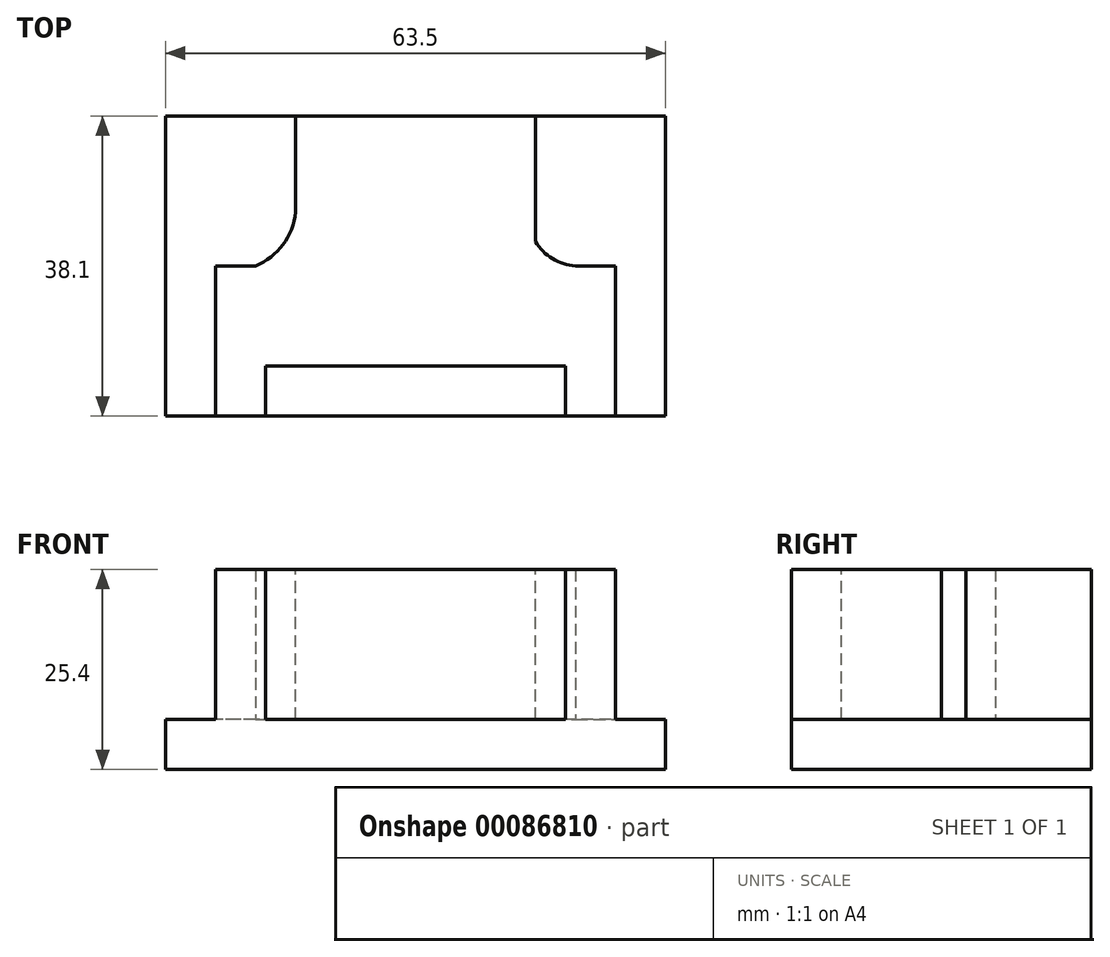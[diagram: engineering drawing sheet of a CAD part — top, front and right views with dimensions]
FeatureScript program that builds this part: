
annotation { "Feature Type Name" : "Feature", "Feature Type Description" : "" }
export const myFeature = defineFeature(function(context is Context, id is Id, definition is map)
    precondition{}
    {
        {
            var Q0;
            Q0=qCreatedBy(makeId("Top.planeOp"),FACE);
            var sketch = newSketch(context, id + "F0", { "sketchPlane" : qUnion([Q0])});
            skLineSegment(sketch, "E0", {"start": v(-31.75, 19.05) * mm, "end": v(-31.75, -19.05) * mm});
            skLineSegment(sketch, "E1", {"start": v(-31.75, -19.05) * mm, "end": v(31.75, -19.05) * mm});
            skLineSegment(sketch, "E2", {"start": v(31.75, -19.05) * mm, "end": v(31.75, 19.05) * mm});
            skLineSegment(sketch, "E3", {"start": v(31.75, 19.05) * mm, "end": v(-31.75, 19.05) * mm});
            skLineSegment(sketch, "E4", {"start": v(-31.75, 0) * mm, "end": v(31.75, 0) * mm, "construction": true});
            skLineSegment(sketch, "E5", {"start": v(0, 19.05) * mm, "end": v(0, 0) * mm, "construction": true});
            skPoint(sketch, "E6", {"position": v(0, 0) * mm});
            skSolve(sketch);
        }
        {
            var Q0;
            Q0=makeQuery(id+"F0.imprint","IMPRINT",FACE,{"disambiguationData":[TD([[makeQuery(id+"F0.imprint","IMPRINT",EDGE,{"derivedFrom":sQuery(id+"F0.wireOp",EDGE,"E0")}),1.0]])]});
            extrude(context, id + "F1", {"entities" : qUnion([Q0]), "depth" : 6.35 * mm});
        }
        {
            var Q0;
            Q0=makeQuery(id+"F1.opExtrude","CAP_FACE",FACE,{"disambiguationData":[OSD([sQuery(id+"F0.wireOp",EDGE,"E0"),sQuery(id+"F0.wireOp",EDGE,"E1"),sQuery(id+"F0.wireOp",EDGE,"E2"),sQuery(id+"F0.wireOp",EDGE,"E3")])],"isStart":false});
            var sketch = newSketch(context, id + "F2", { "sketchPlane" : qUnion([Q0])});
            skLineSegment(sketch, "E7.bottom", {"start": v(-25.4, -19.05) * mm, "end": v(25.4, -19.05) * mm});
            skLineSegment(sketch, "E7.top", {"start": v(-25.4, 19.05) * mm, "end": v(25.4, 19.05) * mm});
            skLineSegment(sketch, "E7.left", {"start": v(-25.4, -19.05) * mm, "end": v(-25.4, 19.05) * mm});
            skLineSegment(sketch, "E7.right", {"start": v(25.4, -19.05) * mm, "end": v(25.4, 19.05) * mm});
            skSolve(sketch);
        }
        {
            var Q0;
            Q0=makeQuery(id+"F2.imprint","IMPRINT",FACE,{"disambiguationData":[TD([[makeQuery(id+"F2.imprint","IMPRINT",EDGE,{"derivedFrom":sQuery(id+"F2.wireOp",EDGE,"E7.bottom")}),1.0]])]});
            extrude(context, id + "F3", {"entities" : qUnion([Q0]), "operationType" : NewBodyOperationType.ADD, "depth" : 19.05 * mm});
        }
        {
            var Q0;
            Q0=makeQuery(id+"F3.opExtrude","CAP_FACE",FACE,{"disambiguationData":[OSD([sQuery(id+"F2.wireOp",EDGE,"E7.bottom"),sQuery(id+"F2.wireOp",EDGE,"E7.top"),sQuery(id+"F2.wireOp",EDGE,"E7.left"),sQuery(id+"F2.wireOp",EDGE,"E7.right")])],"isStart":false});
            var sketch = newSketch(context, id + "F4", { "sketchPlane" : qUnion([Q0])});
            skLineSegment(sketch, "E8.bottom", {"start": v(-19.05, -19.05) * mm, "end": v(19.05, -19.05) * mm});
            skLineSegment(sketch, "E8.top", {"start": v(-19.05, -12.7) * mm, "end": v(19.05, -12.7) * mm});
            skLineSegment(sketch, "E8.left", {"start": v(-19.05, -19.05) * mm, "end": v(-19.05, -12.7) * mm});
            skLineSegment(sketch, "E8.right", {"start": v(19.05, -19.05) * mm, "end": v(19.05, -12.7) * mm});
            skSolve(sketch);
        }
        {
            var Q0;
            Q0=makeQuery(id+"F4.imprint","IMPRINT",FACE,{"disambiguationData":[TD([[makeQuery(id+"F4.imprint","IMPRINT",EDGE,{"derivedFrom":sQuery(id+"F4.wireOp",EDGE,"E8.bottom")}),1.0]])]});
            extrude(context, id + "F5", {"entities" : qUnion([Q0]), "operationType" : NewBodyOperationType.REMOVE, "oppositeDirection" : true, "depth" : 19.05 * mm});
        }
        {
            var Q0;
            Q0=makeQuery(id+"F3.opExtrude","CAP_FACE",FACE,{"disambiguationData":[OSD([sQuery(id+"F2.wireOp",EDGE,"E7.bottom"),sQuery(id+"F2.wireOp",EDGE,"E7.top"),sQuery(id+"F2.wireOp",EDGE,"E7.left"),sQuery(id+"F2.wireOp",EDGE,"E7.right")])],"isStart":false});
            var sketch = newSketch(context, id + "F6", { "sketchPlane" : qUnion([Q0])});
            skLineSegment(sketch, "E9.bottom", {"start": v(-15.24, 19.05) * mm, "end": v(-25.4, 19.05) * mm});
            skLineSegment(sketch, "E9.top", {"start": v(-15.24, 0) * mm, "end": v(-25.4, 0) * mm});
            skLineSegment(sketch, "E9.left", {"start": v(-15.24, 19.05) * mm, "end": v(-15.24, 0) * mm});
            skLineSegment(sketch, "E9.right", {"start": v(-25.4, 19.05) * mm, "end": v(-25.4, 0) * mm});
            skLineSegment(sketch, "E10.MirrorCS", {"start": v(15.24, 19.05) * mm, "end": v(15.24, 0) * mm});
            skLineSegment(sketch, "E11.MirrorCS", {"start": v(15.24, 0) * mm, "end": v(25.4, 0) * mm});
            skSolve(sketch);
        }
        {
            var Q0;
            Q0=makeQuery(id+"F6.imprint","IMPRINT",FACE,{"disambiguationData":[TD([[makeQuery(id+"F6.imprint","IMPRINT",EDGE,{"derivedFrom":sQuery(id+"F6.wireOp",EDGE,"E9.bottom")}),1.0]])]});
            extrude(context, id + "F7", {"entities" : qUnion([Q0]), "operationType" : NewBodyOperationType.REMOVE, "oppositeDirection" : true, "depth" : 19.05 * mm});
        }
        {
            var Q0;
            {var subQ0=sQuery(id+"F6.wireOp",EDGE,"E10.MirrorCS");Q0=makeQuery(id+"F6.imprint","IMPRINT",FACE,{"disambiguationData":[TD([[makeQuery(id+"F6.imprint","IMPRINT",EDGE,{"derivedFrom":subQ0}),1.0]])]});}
            extrude(context, id + "F8", {"entities" : qUnion([Q0]), "operationType" : NewBodyOperationType.REMOVE, "oppositeDirection" : true, "depth" : 19.05 * mm});
        }
        {
            var Q0;
            {var subQ0=sQuery(id+"F0.wireOp",EDGE,"E3");var subQ1=sQuery(id+"F0.wireOp",EDGE,"E1");var subQ2=sQuery(id+"F0.wireOp",EDGE,"E0");Q0=makeQuery(id+"F7.boolean.opBoolean","MERGE",FACE,{"derivedFrom":[makeQuery(id+"F3.boolean.opBoolean","SPLIT",FACE,{"disambiguationData":[TD([makeQuery(id+"F1.opExtrude","SWEPT_FACE",FACE,{"disambiguationData":[OSD([subQ2])]})])],"derivedFrom":makeQuery(id+"F1.opExtrude","CAP_FACE",FACE,{"disambiguationData":[OSD([subQ2,subQ1,sQuery(id+"F0.wireOp",EDGE,"E2"),subQ0])],"isStart":false})}),makeQuery(id+"F7.opExtrude","CAP_FACE",FACE,{"disambiguationData":[OSD([sQuery(id+"F6.wireOp",EDGE,"E9.bottom"),sQuery(id+"F6.wireOp",EDGE,"E9.top"),sQuery(id+"F6.wireOp",EDGE,"E9.left"),sQuery(id+"F6.wireOp",EDGE,"E9.right")])],"isStart":false})]});}
            var sketch = newSketch(context, id + "F9", { "sketchPlane" : qUnion([Q0])});
            skArc(sketch, "E12", {"start": v(-20.32, 0) * mm, "mid": v(-16.84, 2.72) * mm, "end": v(-15.24, 6.83) * mm});
            skSolve(sketch);
        }
        {
            var Q0;
            Q0 = qSketchRegion(id + "F9", true);
            var Q1;
            {var subQ0=sQuery(id+"F9.wireOp",EDGE,"E12");Q1=makeQuery(id+"F9.imprint","IMPRINT",FACE,{"disambiguationData":[TD([[makeQuery(id+"F9.imprint","IMPRINT",EDGE,{"derivedFrom":subQ0}),-1.0]])]});}
            extrude(context, id + "F10", {"entities" : qUnion([Q0, Q1]), "operationType" : NewBodyOperationType.ADD, "depth" : 19.05 * mm});
        }
        {
            var Q0;
            {var subQ0=sQuery(id+"F2.wireOp",EDGE,"E7.right");var subQ1=sQuery(id+"F2.wireOp",EDGE,"E7.top");var subQ2=sQuery(id+"F0.wireOp",EDGE,"E3");var subQ3=sQuery(id+"F0.wireOp",EDGE,"E2");var subQ4=sQuery(id+"F0.wireOp",EDGE,"E1");Q0=makeQuery(id+"F8.boolean.opBoolean","MERGE",FACE,{"derivedFrom":[makeQuery(id+"F3.boolean.opBoolean","SPLIT",FACE,{"disambiguationData":[TD([makeQuery(id+"F1.opExtrude","SWEPT_FACE",FACE,{"disambiguationData":[OSD([subQ3])]})])],"derivedFrom":makeQuery(id+"F1.opExtrude","CAP_FACE",FACE,{"disambiguationData":[OSD([sQuery(id+"F0.wireOp",EDGE,"E0"),subQ4,subQ3,subQ2])],"isStart":false})}),makeQuery(id+"F8.opExtrude","CAP_FACE",FACE,{"disambiguationData":[OSD([subQ1,subQ0,sQuery(id+"F6.wireOp",EDGE,"E10.MirrorCS"),sQuery(id+"F6.wireOp",EDGE,"E11.MirrorCS")])],"isStart":false})]});}
            var sketch = newSketch(context, id + "F11", { "sketchPlane" : qUnion([Q0])});
            skArc(sketch, "E13", {"start": v(15.24, 9.53) * mm, "mid": v(15.11, 3.34) * mm, "end": v(20.32, 0) * mm});
            skSolve(sketch);
        }
        {
            var Q0;
            {var subQ0=sQuery(id+"F11.wireOp",EDGE,"E13");var subQ1=makeQuery(id+"F8.boolean.opBoolean","COPY",EDGE,{"derivedFrom":makeQuery(id+"F8.opExtrude","CAP_EDGE",EDGE,{"disambiguationData":[OSD([sQuery(id+"F6.wireOp",EDGE,"E11.MirrorCS")])],"isStart":false})});var subQ2=makeQuery(id+"F11.imprint","INTERSECT",VERTEX,{"derivedFrom":[subQ1,subQ0]});Q0=makeQuery(id+"F11.imprint","IMPRINT",FACE,{"disambiguationData":[TD([[makeQuery(id+"F11.imprint","IMPRINT",EDGE,{"disambiguationData":[TD([[subQ2,1.0]])],"derivedFrom":subQ0}),-1.0]])]});}
            extrude(context, id + "F12", {"entities" : qUnion([Q0]), "operationType" : NewBodyOperationType.ADD, "depth" : 19.05 * mm});
        }
    });
